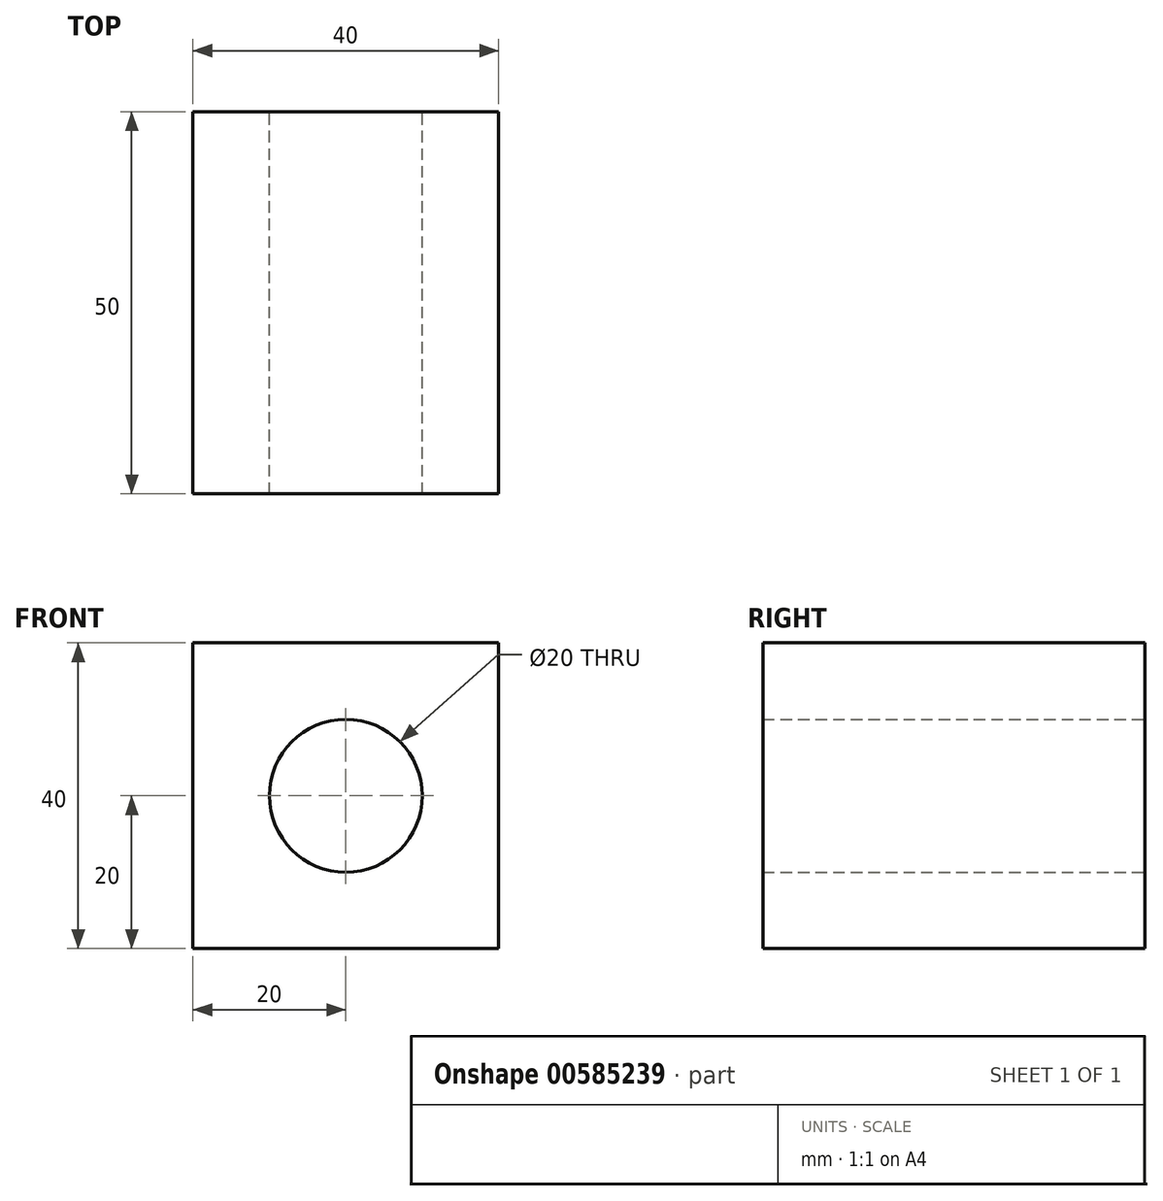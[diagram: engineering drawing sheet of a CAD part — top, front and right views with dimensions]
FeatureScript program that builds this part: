
annotation { "Feature Type Name" : "Feature", "Feature Type Description" : "" }
export const myFeature = defineFeature(function(context is Context, id is Id, definition is map)
    precondition{}
    {
        {
            var Q0;
            Q0=qCreatedBy(makeId("Front.planeOp"),FACE);
            var sketch = newSketch(context, id + "F0", { "sketchPlane" : qUnion([Q0])});
            skLineSegment(sketch, "E0.bottom", {"start": v(-20, 20) * mm, "end": v(20, 20) * mm});
            skLineSegment(sketch, "E0.top", {"start": v(-20, -20) * mm, "end": v(20, -20) * mm});
            skLineSegment(sketch, "E0.left", {"start": v(-20, 20) * mm, "end": v(-20, -20) * mm});
            skLineSegment(sketch, "E0.right", {"start": v(20, 20) * mm, "end": v(20, -20) * mm});
            skSolve(sketch);
        }
        {
            var Q0;
            Q0 = qSketchRegion(id + "F0", true);
            extrude(context, id + "F1", {"entities" : qUnion([Q0]), "depth" : 50 * mm, "offsetDistance" : 25 * mm});
        }
        {
            var Q0;
            Q0=qCreatedBy(makeId("Right.planeOp"),FACE);
            var sketch = newSketch(context, id + "F2", { "sketchPlane" : qUnion([Q0])});
            skLineSegment(sketch, "E1.bottom", {"start": v(-50, 10) * mm, "end": v(0, 10) * mm});
            skLineSegment(sketch, "E1.top", {"start": v(-50, 0) * mm, "end": v(0, 0) * mm});
            skLineSegment(sketch, "E1.left", {"start": v(-50, 10) * mm, "end": v(-50, 0) * mm});
            skLineSegment(sketch, "E1.right", {"start": v(0, 10) * mm, "end": v(0, 0) * mm});
            skLineSegment(sketch, "E2", {"start": v(-70.3, 0) * mm, "end": v(27.55, 0) * mm, "construction": true});
            skSolve(sketch);
        }
        {
            var Q0;
            Q0 = qSketchRegion(id + "F2", true);
            var Q1;
            Q1=sQuery(id+"F2.wireOp",EDGE,"E2");
            revolve(context, id + "F3", {"operationType" : NewBodyOperationType.REMOVE, "entities" : qUnion([Q0]), "axis" : qUnion([Q1]), "revolveType" : RevolveType.FULL, "oppositeDirection" : true});
        }
    });
